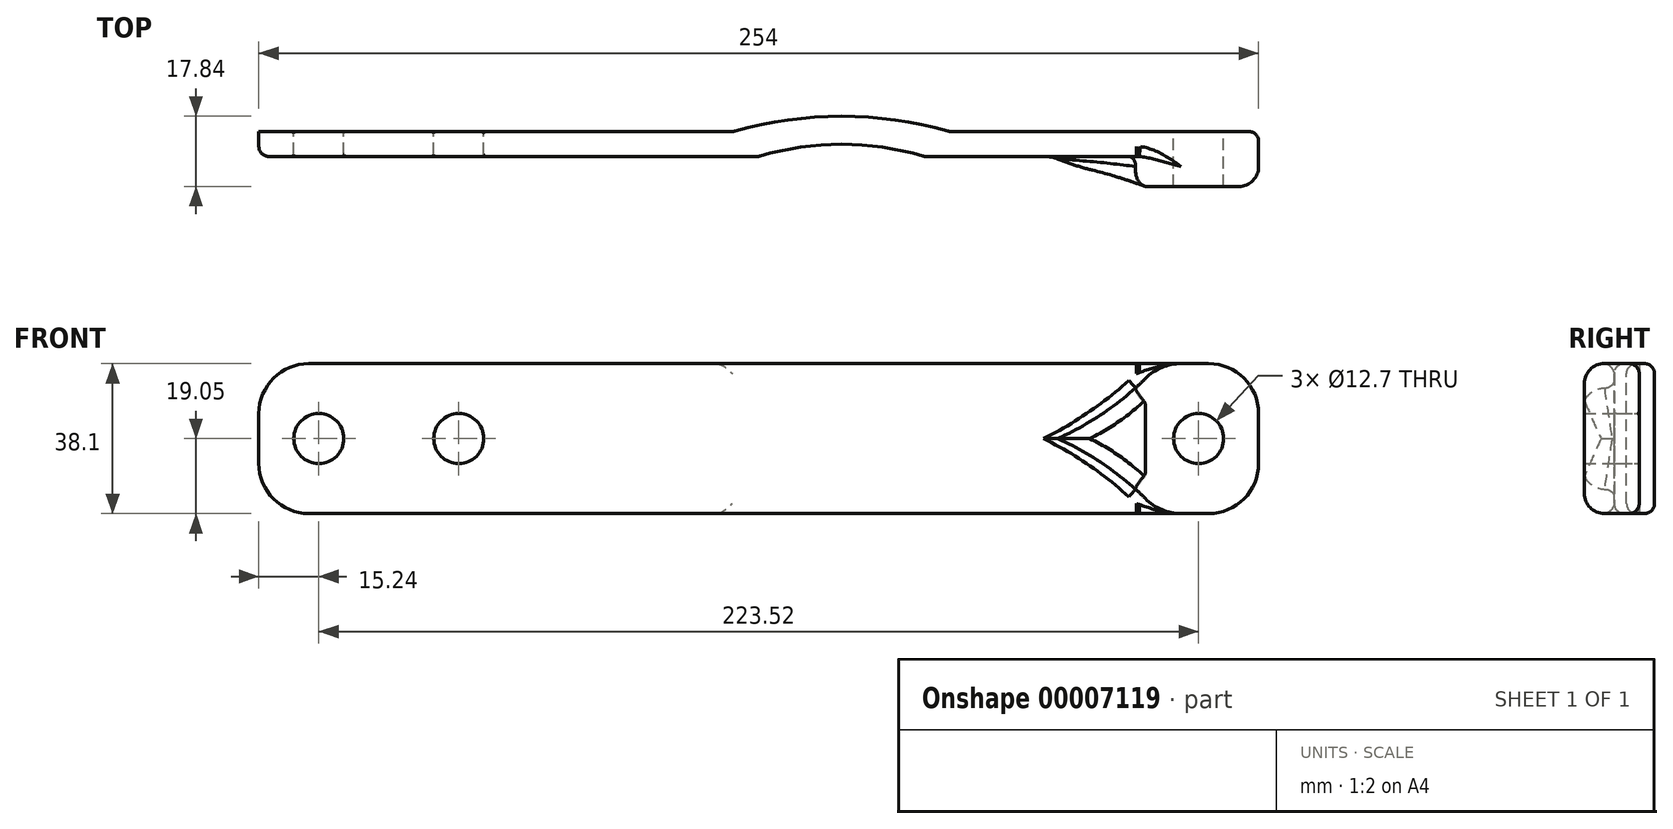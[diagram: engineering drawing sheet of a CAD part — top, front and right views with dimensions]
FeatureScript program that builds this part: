
annotation { "Feature Type Name" : "Feature", "Feature Type Description" : "" }
export const myFeature = defineFeature(function(context is Context, id is Id, definition is map)
    precondition{}
    {
        {
            var Q0;
            Q0=qCreatedBy(makeId("Front.planeOp"),FACE);
            var sketch = newSketch(context, id + "F0", { "sketchPlane" : qUnion([Q0])});
            skLineSegment(sketch, "E0.bottom", {"start": v(-114.3, 19.05) * mm, "end": v(114.3, 19.05) * mm});
            skLineSegment(sketch, "E0.top", {"start": v(-114.3, -19.05) * mm, "end": v(114.3, -19.05) * mm});
            skLineSegment(sketch, "E0.left", {"start": v(-127, 6.35) * mm, "end": v(-127, -6.35) * mm});
            skLineSegment(sketch, "E0.right", {"start": v(127, 6.35) * mm, "end": v(127, -6.35) * mm});
            skPoint(sketch, "E1.visualSharp", {"position": v(-127, 19.05) * mm});
            skArc(sketch, "E1.filletArc", {"start": v(-114.3, 19.05) * mm, "mid": v(-123.28, 15.33) * mm, "end": v(-127, 6.35) * mm});
            skPoint(sketch, "E2.visualSharp", {"position": v(-127, -19.05) * mm});
            skArc(sketch, "E2.filletArc", {"start": v(-127, -6.35) * mm, "mid": v(-123.28, -15.33) * mm, "end": v(-114.3, -19.05) * mm});
            skPoint(sketch, "E3.visualSharp", {"position": v(127, -19.05) * mm});
            skArc(sketch, "E3.filletArc", {"start": v(114.3, -19.05) * mm, "mid": v(123.28, -15.33) * mm, "end": v(127, -6.35) * mm});
            skPoint(sketch, "E4.visualSharp", {"position": v(127, 19.05) * mm});
            skArc(sketch, "E4.filletArc", {"start": v(127, 6.35) * mm, "mid": v(123.28, 15.33) * mm, "end": v(114.3, 19.05) * mm});
            skCircle(sketch, "E5", {"center": v(-111.76, 0) * mm, "radius": 6.35 * mm});
            skCircle(sketch, "E6", {"center": v(-76.2, 0) * mm, "radius": 6.35 * mm});
            skCircle(sketch, "E7", {"center": v(111.76, 0) * mm, "radius": 6.35 * mm});
            skSolve(sketch);
        }
        {
            var Q0;
            Q0=makeQuery(id+"F0.imprint","IMPRINT",FACE,{"disambiguationData":[TD([[makeQuery(id+"F0.imprint","IMPRINT",EDGE,{"derivedFrom":sQuery(id+"F0.wireOp",EDGE,"E0.bottom")}),-1.0]])]});
            extrude(context, id + "F1", {"entities" : qUnion([Q0]), "depth" : 6.35 * mm});
        }
        {
            var Q0;
            Q0=makeQuery(id+"F1.opExtrude","CAP_FACE",FACE,{"disambiguationData":[OSD([sQuery(id+"F0.wireOp",EDGE,"E0.bottom"),sQuery(id+"F0.wireOp",EDGE,"E0.top"),sQuery(id+"F0.wireOp",EDGE,"E0.left"),sQuery(id+"F0.wireOp",EDGE,"E0.right"),sQuery(id+"F0.wireOp",EDGE,"E1.filletArc"),sQuery(id+"F0.wireOp",EDGE,"E2.filletArc"),sQuery(id+"F0.wireOp",EDGE,"E3.filletArc"),sQuery(id+"F0.wireOp",EDGE,"E4.filletArc"),sQuery(id+"F0.wireOp",EDGE,"E5"),sQuery(id+"F0.wireOp",EDGE,"E6"),sQuery(id+"F0.wireOp",EDGE,"E7")])],"isStart":false});
            var sketch = newSketch(context, id + "F2", { "sketchPlane" : qUnion([Q0])});
            skLineSegment(sketch, "E8", {"start": v(0, 0) * mm, "end": v(111.76, 0) * mm, "construction": true});
            skArc(sketch, "E9", {"start": v(98.22, -15.24) * mm, "mid": v(81.17, -3.77) * mm, "end": v(60.96, 0) * mm});
            skArc(sketch, "E10.0.MirrorCS", {"start": v(98.22, 15.24) * mm, "mid": v(81.17, 3.77) * mm, "end": v(60.96, 0) * mm});
            skLineSegment(sketch, "E11", {"start": v(107.3, 19.05) * mm, "end": v(114.3, 19.05) * mm});
            skArc(sketch, "E12", {"start": v(127, 6.35) * mm, "mid": v(123.28, 15.33) * mm, "end": v(114.3, 19.05) * mm});
            skArc(sketch, "E13", {"start": v(114.3, -19.05) * mm, "mid": v(123.28, -15.33) * mm, "end": v(127, -6.35) * mm});
            skLineSegment(sketch, "E14", {"start": v(127, -6.35) * mm, "end": v(127, 6.35) * mm});
            skLineSegment(sketch, "E15", {"start": v(114.3, -19.05) * mm, "end": v(107.3, -19.05) * mm});
            skCircle(sketch, "E16", {"center": v(111.76, 0) * mm, "radius": 12.7 * mm});
            skPoint(sketch, "E17.visualSharp", {"position": v(101.6, 19.05) * mm});
            skArc(sketch, "E17.filletArc", {"start": v(107.3, 19.05) * mm, "mid": v(102.37, 18.06) * mm, "end": v(98.22, 15.24) * mm});
            skPoint(sketch, "E18.visualSharp", {"position": v(101.6, -19.05) * mm});
            skArc(sketch, "E18.filletArc", {"start": v(98.22, -15.24) * mm, "mid": v(102.37, -18.06) * mm, "end": v(107.3, -19.05) * mm});
            skSolve(sketch);
        }
        {
            var Q0;
            Q0=makeQuery(id+"F2.imprint","IMPRINT",FACE,{"disambiguationData":[TD([[makeQuery(id+"F2.imprint","IMPRINT",EDGE,{"derivedFrom":sQuery(id+"F2.wireOp",EDGE,"E16")}),1.0]])]});
            extrude(context, id + "F3", {"entities" : qUnion([Q0]), "operationType" : NewBodyOperationType.ADD, "depth" : 7.62 * mm});
        }
        {
            var Q0;
            Q0=makeQuery(id+"F2.imprint","IMPRINT",FACE,{"disambiguationData":[TD([[makeQuery(id+"F2.imprint","IMPRINT",EDGE,{"derivedFrom":sQuery(id+"F2.wireOp",EDGE,"E11")}),-1.0]])]});
            extrude(context, id + "F4", {"entities" : qUnion([Q0]), "operationType" : NewBodyOperationType.ADD, "depth" : 7.62 * mm});
        }
        {
            var Q0;
            Q0=qCreatedBy(makeId("Top.planeOp"),FACE);
            var sketch = newSketch(context, id + "F5", { "sketchPlane" : qUnion([Q0])});
            skPoint(sketch, "E19", {"position": v(62.91, -6.35) * mm});
            skPoint(sketch, "E20", {"position": v(98.22, -13.97) * mm});
            skLineSegment(sketch, "E21", {"start": v(62.91, -6.35) * mm, "end": v(62.91, -13.97) * mm});
            skLineSegment(sketch, "E22", {"start": v(62.91, -13.97) * mm, "end": v(98.22, -13.97) * mm});
            skArc(sketch, "E23", {"start": v(98.22, -13.97) * mm, "mid": v(80.84, -8.9) * mm, "end": v(62.91, -6.35) * mm});
            skSolve(sketch);
        }
        {
            var Q0;
            Q0 = qSketchRegion(id + "F5", true);
            extrude(context, id + "F6", {"entities" : qUnion([Q0]), "operationType" : NewBodyOperationType.REMOVE, "endBound" : BoundingType.SYMMETRIC, "oppositeDirection" : true, "depth" : 50.8 * mm});
        }
        {
            var Q0;
            Q0=makeQuery(id+"F4.opExtrude","CAP_EDGE",EDGE,{"disambiguationData":[OSD([sQuery(id+"F2.wireOp",EDGE,"E18.filletArc")])],"isStart":false});
            var Q1;
            Q1=makeQuery(id+"F6.boolean.opBoolean","INTERSECT",EDGE,{"derivedFrom":[makeQuery(id+"F4.opExtrude","SWEPT_FACE",FACE,{"disambiguationData":[OSD([sQuery(id+"F2.wireOp",EDGE,"E9")])]}),makeQuery(id+"F6.opExtrude","SWEPT_FACE",FACE,{"disambiguationData":[OSD([sQuery(id+"F5.wireOp",EDGE,"E23")])]})]});
            var Q2;
            Q2=makeQuery(id+"F6.boolean.opBoolean","INTERSECT",EDGE,{"derivedFrom":[makeQuery(id+"F4.opExtrude","SWEPT_FACE",FACE,{"disambiguationData":[OSD([sQuery(id+"F2.wireOp",EDGE,"E10.0.MirrorCS")])]}),makeQuery(id+"F6.opExtrude","SWEPT_FACE",FACE,{"disambiguationData":[OSD([sQuery(id+"F5.wireOp",EDGE,"E23")])]})]});
            fillet(context, id + "F7", {"entities" : qUnion([Q0, Q1, Q2]), "radius" : 5.08 * mm, "tangentPropagation" : true, "allowEdgeOverflow" : false});
        }
        {
            var Q0;
            Q0=makeQuery(id+"F1.opExtrude","CAP_EDGE",EDGE,{"disambiguationData":[OSD([sQuery(id+"F0.wireOp",EDGE,"E5")])],"isStart":false});
            var Q1;
            Q1=makeQuery(id+"F1.opExtrude","CAP_EDGE",EDGE,{"disambiguationData":[OSD([sQuery(id+"F0.wireOp",EDGE,"E5")])],"isStart":true});
            var Q2;
            Q2=makeQuery(id+"F1.opExtrude","CAP_EDGE",EDGE,{"disambiguationData":[OSD([sQuery(id+"F0.wireOp",EDGE,"E6")])],"isStart":false});
            var Q3;
            Q3=makeQuery(id+"F1.opExtrude","CAP_EDGE",EDGE,{"disambiguationData":[OSD([sQuery(id+"F0.wireOp",EDGE,"E6")])],"isStart":true});
            fillet(context, id + "F8", {"entities" : qUnion([Q0, Q1, Q2, Q3]), "radius" : 0.5 * mm, "tangentPropagation" : true, "allowEdgeOverflow" : false});
        }
        {
            var Q0;
            Q0=makeQuery(id+"F4.boolean.opBoolean","MERGE",FACE,{"derivedFrom":[makeQuery(id+"F1.opExtrude","SWEPT_FACE",FACE,{"disambiguationData":[OSD([sQuery(id+"F0.wireOp",EDGE,"E0.bottom")])]}),makeQuery(id+"F4.opExtrude","SWEPT_FACE",FACE,{"disambiguationData":[OSD([sQuery(id+"F2.wireOp",EDGE,"E11")])]})]});
            var sketch = newSketch(context, id + "F9", { "sketchPlane" : qUnion([Q0])});
            skLineSegment(sketch, "E24", {"start": v(-6.35, 0) * mm, "end": v(48.4, 0) * mm});
            skLineSegment(sketch, "E25.0", {"start": v(92.87, -6.35) * mm, "end": v(-123.2, -6.35) * mm});
            skLineSegment(sketch, "E26", {"start": v(7.62, -6.35) * mm, "end": v(48.03, -6.35) * mm});
            skLineSegment(sketch, "E27", {"start": v(0, -6.35) * mm, "end": v(86.16, -6.35) * mm});
            skArc(sketch, "E28", {"start": v(42.06, -6.35) * mm, "mid": v(21.03, -3.22) * mm, "end": v(0, -6.35) * mm});
            skPoint(sketch, "E29", {"position": v(42.06, 0) * mm});
            skPoint(sketch, "E30", {"position": v(55.26, 0) * mm});
            skPoint(sketch, "E31", {"position": v(-11.78, 0) * mm});
            skArc(sketch, "E32", {"start": v(48.4, 0) * mm, "mid": v(21.03, 3.87) * mm, "end": v(-6.35, 0) * mm});
            skLineSegment(sketch, "E33", {"start": v(0, 0) * mm, "end": v(0, -18.91) * mm, "construction": true});
            skPoint(sketch, "E33.endSnap0", {"position": v(0, 0) * mm});
            skSolve(sketch);
        }
        {
            var Q0;
            Q0=makeQuery(id+"F9.imprint","IMPRINT",FACE,{"disambiguationData":[TD([[makeQuery(id+"F9.imprint","IMPRINT",EDGE,{"derivedFrom":sQuery(id+"F9.wireOp",EDGE,"E24")}),1.0]])]});
            extrude(context, id + "F10", {"entities" : qUnion([Q0]), "operationType" : NewBodyOperationType.ADD, "oppositeDirection" : true, "depth" : 38.1 * mm});
        }
        {
            var Q0;
            {var subQ0=sQuery(id+"F9.wireOp",EDGE,"E28");Q0=makeQuery(id+"F9.imprint","IMPRINT",FACE,{"disambiguationData":[TD([[makeQuery(id+"F9.imprint","IMPRINT",EDGE,{"derivedFrom":subQ0}),1.0]])]});}
            extrude(context, id + "F11", {"entities" : qUnion([Q0]), "operationType" : NewBodyOperationType.REMOVE, "oppositeDirection" : true, "depth" : 38.1 * mm});
        }
        {
            var Q0;
            {var subQ2=sQuery(id+"F0.wireOp",EDGE,"E6");var subQ3=sQuery(id+"F0.wireOp",EDGE,"E5");var subQ4=sQuery(id+"F0.wireOp",EDGE,"E2.filletArc");var subQ5=sQuery(id+"F0.wireOp",EDGE,"E0.bottom");var subQ6=sQuery(id+"F0.wireOp",EDGE,"E0.top");var subQ7=sQuery(id+"F0.wireOp",EDGE,"E0.left");var subQ8=sQuery(id+"F0.wireOp",EDGE,"E1.filletArc");Q0=makeQuery(id+"F11.boolean.opBoolean","SPLIT",FACE,{"disambiguationData":[TD([makeQuery(id+"F1.opExtrude","SWEPT_FACE",FACE,{"disambiguationData":[OSD([subQ7])]})])],"derivedFrom":makeQuery(id+"F1.opExtrude","CAP_FACE",FACE,{"disambiguationData":[OSD([subQ5,subQ6,subQ7,sQuery(id+"F0.wireOp",EDGE,"E0.right"),subQ8,subQ4,sQuery(id+"F0.wireOp",EDGE,"E3.filletArc"),sQuery(id+"F0.wireOp",EDGE,"E4.filletArc"),subQ3,subQ2,sQuery(id+"F0.wireOp",EDGE,"E7")])],"isStart":false})});}
            var Q1;
            {var subQ4=sQuery(id+"F2.wireOp",EDGE,"E9");var subQ5=sQuery(id+"F0.wireOp",EDGE,"E0.top");var subQ6=sQuery(id+"F0.wireOp",EDGE,"E0.bottom");Q1=makeQuery(id+"F11.boolean.opBoolean","SPLIT",FACE,{"disambiguationData":[TD([makeQuery(id+"F4.opExtrude","SWEPT_FACE",FACE,{"disambiguationData":[OSD([subQ4])]})])],"derivedFrom":makeQuery(id+"F1.opExtrude","CAP_FACE",FACE,{"disambiguationData":[OSD([subQ6,subQ5,sQuery(id+"F0.wireOp",EDGE,"E0.left"),sQuery(id+"F0.wireOp",EDGE,"E0.right"),sQuery(id+"F0.wireOp",EDGE,"E1.filletArc"),sQuery(id+"F0.wireOp",EDGE,"E2.filletArc"),sQuery(id+"F0.wireOp",EDGE,"E3.filletArc"),sQuery(id+"F0.wireOp",EDGE,"E4.filletArc"),sQuery(id+"F0.wireOp",EDGE,"E5"),sQuery(id+"F0.wireOp",EDGE,"E6"),sQuery(id+"F0.wireOp",EDGE,"E7")])],"isStart":false})});}
            var Q2;
            Q2=makeQuery(id+"F11.boolean.opBoolean","COPY",FACE,{"derivedFrom":makeQuery(id+"F11.opExtrude","SWEPT_FACE",FACE,{"disambiguationData":[OSD([sQuery(id+"F9.wireOp",EDGE,"E28")])]})});
            var Q3;
            {var subQ0=sQuery(id+"F0.wireOp",EDGE,"E4.filletArc");var subQ1=sQuery(id+"F0.wireOp",EDGE,"E0.bottom");Q3=makeQuery(id+"F10.boolean.opBoolean","SPLIT",EDGE,{"disambiguationData":[TD([makeQuery(id+"F1.opExtrude","SWEPT_FACE",FACE,{"disambiguationData":[OSD([subQ0])]})])],"derivedFrom":makeQuery(id+"F1.opExtrude","CAP_EDGE",EDGE,{"disambiguationData":[OSD([subQ1])],"isStart":true})});}
            var Q4;
            Q4=makeQuery(id+"F10.opExtrude","SWEPT_FACE",FACE,{"disambiguationData":[OSD([sQuery(id+"F9.wireOp",EDGE,"E32")])]});
            fillet(context, id + "F12", {"entities" : qUnion([Q0, Q1, Q2, Q3, Q4]), "radius" : 2.54 * mm, "tangentPropagation" : true, "allowEdgeOverflow" : false});
        }
    });
